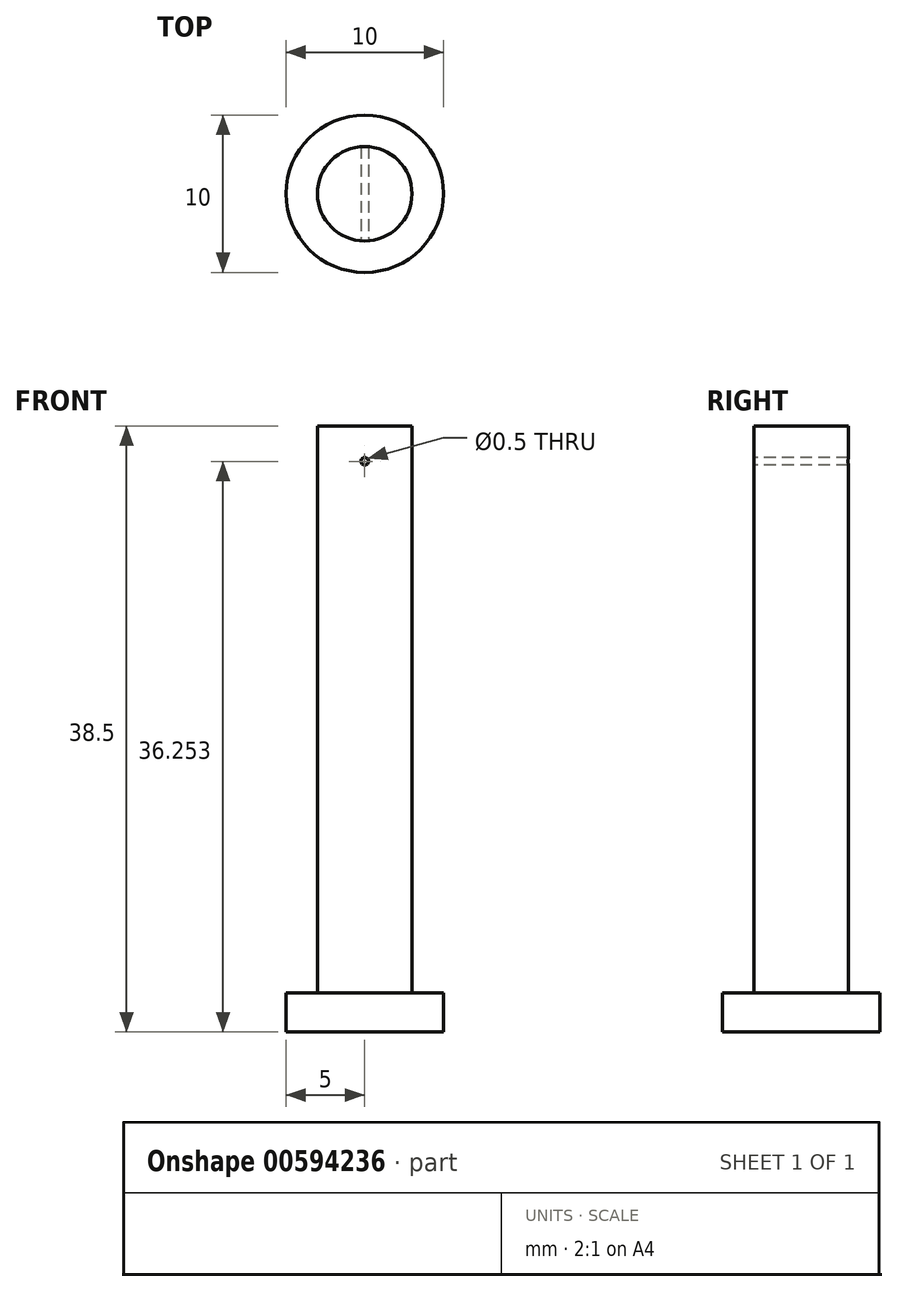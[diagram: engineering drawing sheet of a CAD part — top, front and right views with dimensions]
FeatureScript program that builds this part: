
annotation { "Feature Type Name" : "Feature", "Feature Type Description" : "" }
export const myFeature = defineFeature(function(context is Context, id is Id, definition is map)
    precondition{}
    {
        {
            var Q0;
            Q0=qCreatedBy(makeId("Front.planeOp"),FACE);
            var sketch = newSketch(context, id + "F0", { "sketchPlane" : qUnion([Q0])});
            skLineSegment(sketch, "E0", {"start": v(0, -5.36) * mm, "end": v(5, -5.36) * mm});
            skLineSegment(sketch, "E1", {"start": v(5, -5.36) * mm, "end": v(5, -2.86) * mm});
            skLineSegment(sketch, "E2", {"start": v(5, -2.86) * mm, "end": v(3, -2.86) * mm});
            skLineSegment(sketch, "E3", {"start": v(3, -2.86) * mm, "end": v(3, 33.14) * mm});
            skLineSegment(sketch, "E4", {"start": v(3, 33.14) * mm, "end": v(0, 33.14) * mm});
            skLineSegment(sketch, "E5", {"start": v(0, 33.14) * mm, "end": v(0, -5.36) * mm});
            skSolve(sketch);
        }
        {
            var Q0;
            Q0 = qSketchRegion(id + "F0", true);
            var Q1;
            Q1=sQuery(id+"F0.wireOp",EDGE,"E5");
            revolve(context, id + "F1", {"entities" : qUnion([Q0]), "axis" : qUnion([Q1]), "revolveType" : RevolveType.FULL});
        }
        {
            var Q0;
            Q0=qCreatedBy(makeId("Front.planeOp"),FACE);
            var sketch = newSketch(context, id + "F2", { "sketchPlane" : qUnion([Q0])});
            skCircle(sketch, "E6", {"center": v(0, 30.9) * mm, "radius": 0.25 * mm});
            skSolve(sketch);
        }
        {
            var Q0;
            Q0 = qSketchRegion(id + "F2", true);
            extrude(context, id + "F3", {"entities" : qUnion([Q0]), "operationType" : NewBodyOperationType.REMOVE, "endBound" : BoundingType.SYMMETRIC, "oppositeDirection" : true, "depth" : 25.4 * mm, "offsetDistance" : 25.4 * mm});
        }
    });
